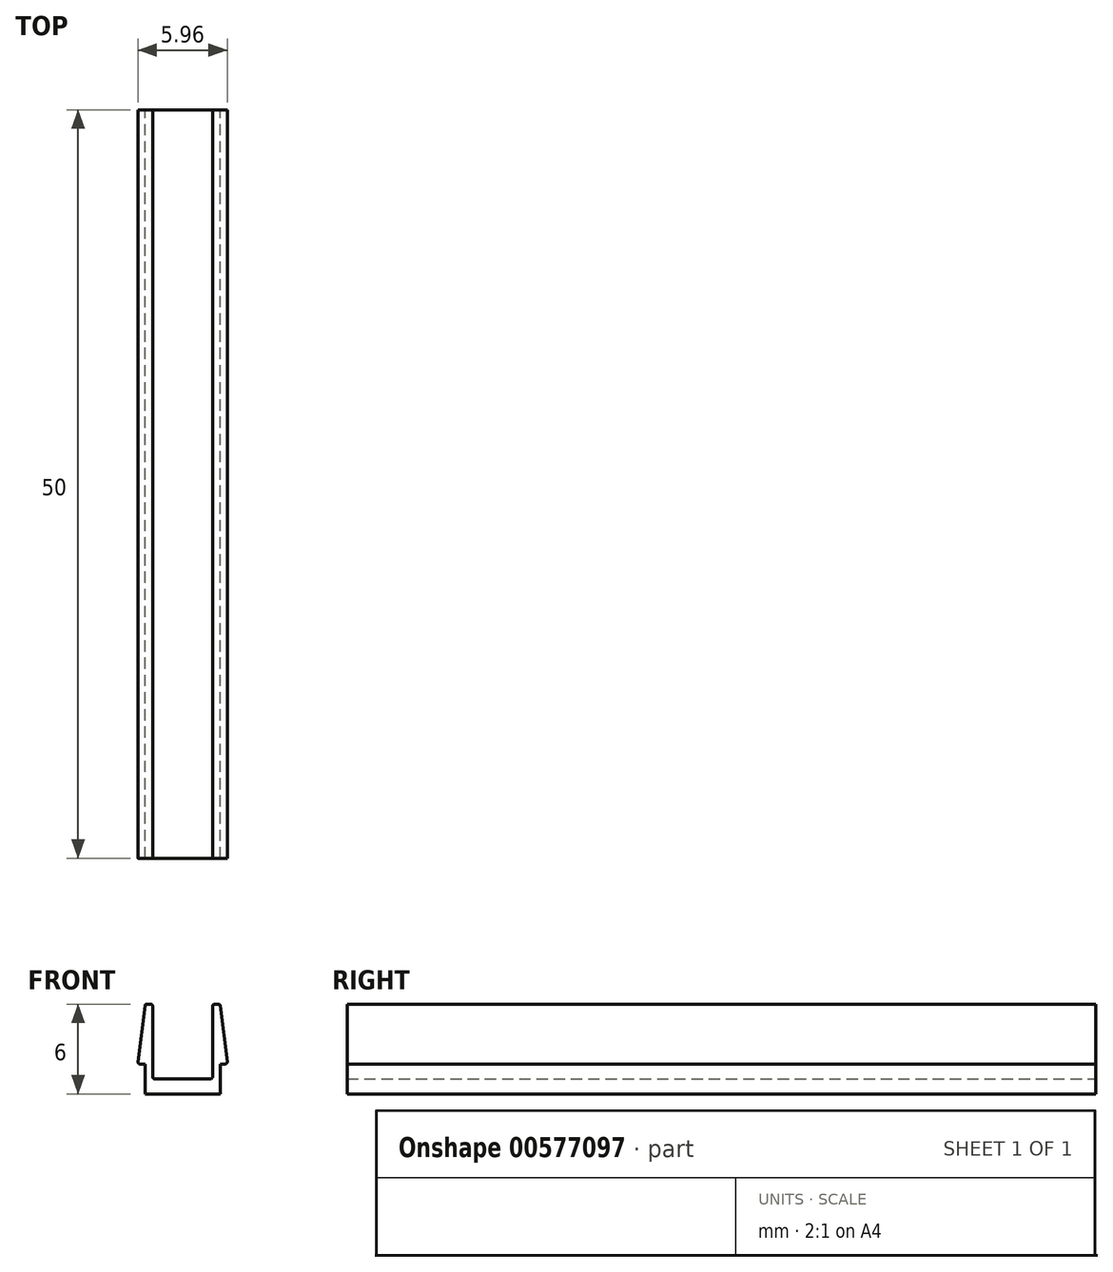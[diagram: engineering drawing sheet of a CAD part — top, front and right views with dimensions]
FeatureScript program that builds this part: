
annotation { "Feature Type Name" : "Feature", "Feature Type Description" : "" }
export const myFeature = defineFeature(function(context is Context, id is Id, definition is map)
    precondition{}
    {
        {
            var Q0;
            Q0=qCreatedBy(makeId("Front.planeOp"),FACE);
            var sketch = newSketch(context, id + "F0", { "sketchPlane" : qUnion([Q0])});
            skLineSegment(sketch, "E0", {"start": v(0, 0) * mm, "end": v(0, 4.16) * mm, "construction": true});
            skLineSegment(sketch, "E1", {"start": v(0, 0) * mm, "end": v(-2.5, 0) * mm});
            skLineSegment(sketch, "E2", {"start": v(-2.5, 0) * mm, "end": v(-2.5, 2) * mm});
            skLineSegment(sketch, "E3", {"start": v(-2.5, 2) * mm, "end": v(-2.84, 2) * mm});
            skLineSegment(sketch, "E4", {"start": v(-2.98, 2.16) * mm, "end": v(-2.52, 5.88) * mm});
            skLineSegment(sketch, "E5", {"start": v(-2.38, 6) * mm, "end": v(-2.14, 6) * mm});
            skLineSegment(sketch, "E6", {"start": v(-2, 5.86) * mm, "end": v(-2, 1.14) * mm});
            skLineSegment(sketch, "E7", {"start": v(-1.86, 1) * mm, "end": v(0, 1) * mm});
            skPoint(sketch, "E8.visualSharp", {"position": v(-2.5, 6) * mm});
            skArc(sketch, "E8.filletArc", {"start": v(-2.38, 6) * mm, "mid": v(-2.47, 5.97) * mm, "end": v(-2.52, 5.88) * mm});
            skPoint(sketch, "E9.visualSharp", {"position": v(-2, 6) * mm});
            skArc(sketch, "E9.filletArc", {"start": v(-2, 5.86) * mm, "mid": v(-2.04, 5.96) * mm, "end": v(-2.14, 6) * mm});
            skPoint(sketch, "E10.visualSharp", {"position": v(-3, 2) * mm});
            skArc(sketch, "E10.filletArc", {"start": v(-2.98, 2.16) * mm, "mid": v(-2.95, 2.05) * mm, "end": v(-2.84, 2) * mm});
            skPoint(sketch, "E11.visualSharp", {"position": v(-2, 2) * mm});
            skArc(sketch, "E11.filletArc", {"start": v(-2, 1.14) * mm, "mid": v(-1.96, 1.04) * mm, "end": v(-1.86, 1) * mm});
            skArc(sketch, "E12.MirrorCS", {"start": v(2.38, 6) * mm, "mid": v(2.47, 5.97) * mm, "end": v(2.52, 5.88) * mm});
            skArc(sketch, "E13.MirrorCS", {"start": v(2, 5.86) * mm, "mid": v(2.04, 5.96) * mm, "end": v(2.14, 6) * mm});
            skArc(sketch, "E14.MirrorCS", {"start": v(2, 1.14) * mm, "mid": v(1.96, 1.04) * mm, "end": v(1.86, 1) * mm});
            skArc(sketch, "E15.MirrorCS", {"start": v(2.98, 2.16) * mm, "mid": v(2.95, 2.05) * mm, "end": v(2.84, 2) * mm});
            skLineSegment(sketch, "E16.MirrorCS", {"start": v(1.86, 1) * mm, "end": v(0, 1) * mm});
            skLineSegment(sketch, "E17.MirrorCS", {"start": v(2.5, 2) * mm, "end": v(2.84, 2) * mm});
            skLineSegment(sketch, "E18.MirrorCS", {"start": v(2.38, 6) * mm, "end": v(2.14, 6) * mm});
            skPoint(sketch, "E19.MirrorP", {"position": v(2, 2) * mm});
            skPoint(sketch, "E20.MirrorP", {"position": v(2.5, 6) * mm});
            skLineSegment(sketch, "E21.MirrorCS", {"start": v(0, 0) * mm, "end": v(2.5, 0) * mm});
            skLineSegment(sketch, "E22.MirrorCS", {"start": v(2.5, 0) * mm, "end": v(2.5, 2) * mm});
            skPoint(sketch, "E23.MirrorP", {"position": v(2, 6) * mm});
            skPoint(sketch, "E24.MirrorP", {"position": v(3, 2) * mm});
            skLineSegment(sketch, "E25.MirrorCS", {"start": v(2, 5.86) * mm, "end": v(2, 1.14) * mm});
            skLineSegment(sketch, "E26.MirrorCS", {"start": v(2.98, 2.16) * mm, "end": v(2.52, 5.88) * mm});
            skSolve(sketch);
        }
        {
            var Q0;
            Q0 = qSketchRegion(id + "F0", true);
            extrude(context, id + "F1", {"entities" : qUnion([Q0]), "depth" : 50 * mm, "offsetDistance" : 25 * mm});
        }
    });
